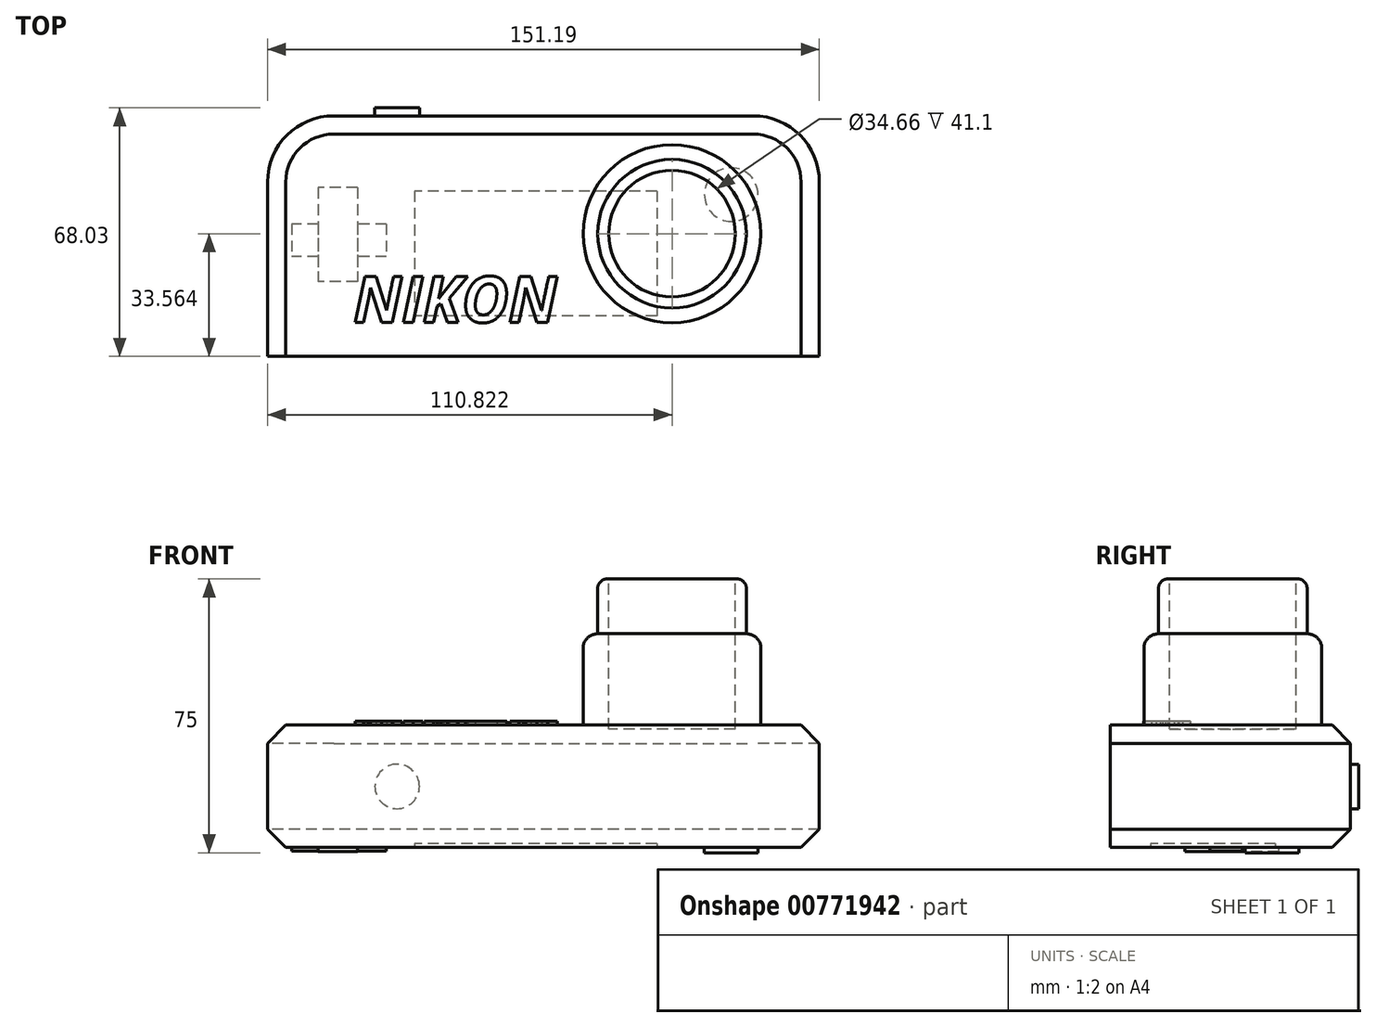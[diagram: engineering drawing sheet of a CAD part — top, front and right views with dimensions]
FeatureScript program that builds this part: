
annotation { "Feature Type Name" : "Feature", "Feature Type Description" : "" }
export const myFeature = defineFeature(function(context is Context, id is Id, definition is map)
    precondition{}
    {
        {
            var Q0;
            Q0=qCreatedBy(makeId("Top.planeOp"),FACE);
            var sketch = newSketch(context, id + "F0", { "sketchPlane" : qUnion([Q0])});
            skLineSegment(sketch, "E0.bottom", {"start": v(0, 0) * mm, "end": v(151.2, 0) * mm});
            skLineSegment(sketch, "E0.top", {"start": v(0, 65.83) * mm, "end": v(151.2, 65.83) * mm});
            skLineSegment(sketch, "E0.left", {"start": v(0, 0) * mm, "end": v(0, 65.83) * mm});
            skLineSegment(sketch, "E0.right", {"start": v(151.2, 0) * mm, "end": v(151.2, 65.83) * mm});
            skSolve(sketch);
        }
        {
            var Q0;
            Q0=makeQuery(id+"F0.imprint","IMPRINT",FACE,{"disambiguationData":[TD([[makeQuery(id+"F0.imprint","IMPRINT",EDGE,{"derivedFrom":sQuery(id+"F0.wireOp",EDGE,"E0.bottom")}),1.0]])]});
            extrude(context, id + "F1", {"entities" : qUnion([Q0]), "depth" : 33.5 * mm, "offsetDistance" : 25 * mm});
        }
        {
            var Q0;
            Q0=makeQuery(id+"F1.opExtrude","CAP_FACE",FACE,{"disambiguationData":[OSD([sQuery(id+"F0.wireOp",EDGE,"E0.bottom"),sQuery(id+"F0.wireOp",EDGE,"E0.top"),sQuery(id+"F0.wireOp",EDGE,"E0.left"),sQuery(id+"F0.wireOp",EDGE,"E0.right")])],"isStart":false});
            var sketch = newSketch(context, id + "F2", { "sketchPlane" : qUnion([Q0])});
            skCircle(sketch, "E1", {"center": v(110.82, 33.56) * mm, "radius": 24.37 * mm});
            skSolve(sketch);
        }
        {
            var Q0;
            Q0 = qSketchRegion(id + "F2", true);
            extrude(context, id + "F3", {"entities" : qUnion([Q0]), "operationType" : NewBodyOperationType.ADD, "depth" : 25 * mm, "offsetDistance" : 25 * mm});
        }
        {
            var Q0;
            Q0=makeQuery(id+"F1.opExtrude","SWEPT_EDGE",EDGE,{"disambiguationData":[OSD([sQuery(id+"F0.wireOp",EDGE,"E0.top"),sQuery(id+"F0.wireOp",EDGE,"E0.right")])]});
            fillet(context, id + "F4", {"entities" : qUnion([Q0]), "radius" : 18.1 * mm, "tangentPropagation" : true, "allowEdgeOverflow" : false});
        }
        {
            var Q0;
            Q0=makeQuery(id+"F1.opExtrude","SWEPT_EDGE",EDGE,{"disambiguationData":[OSD([sQuery(id+"F0.wireOp",EDGE,"E0.top"),sQuery(id+"F0.wireOp",EDGE,"E0.left")])]});
            fillet(context, id + "F5", {"entities" : qUnion([Q0]), "radius" : 18.1 * mm, "tangentPropagation" : true, "allowEdgeOverflow" : false});
        }
        {
            var Q0;
            Q0=makeQuery(id+"F1.opExtrude","CAP_EDGE",EDGE,{"disambiguationData":[OSD([sQuery(id+"F0.wireOp",EDGE,"E0.right")])],"isStart":false});
            var Q1;
            {var subQ0=sQuery(id+"F0.wireOp",EDGE,"E0.right");var subQ1=sQuery(id+"F0.wireOp",EDGE,"E0.top");Q1=makeQuery(id+"F4.opFillet","BLEND_EDGE",EDGE,{"blendedFrom":[makeQuery(id+"F1.opExtrude","SWEPT_EDGE",EDGE,{"disambiguationData":[OSD([subQ1,subQ0])]}),makeQuery(id+"F1.opExtrude","CAP_FACE",FACE,{"disambiguationData":[OSD([sQuery(id+"F0.wireOp",EDGE,"E0.bottom"),subQ1,sQuery(id+"F0.wireOp",EDGE,"E0.left"),subQ0])],"isStart":false})],"blendedInto":[makeQuery(id+"F1.opExtrude","CAP_FACE",FACE,{"disambiguationData":[OSD([sQuery(id+"F0.wireOp",EDGE,"E0.bottom"),subQ1,sQuery(id+"F0.wireOp",EDGE,"E0.left"),subQ0])],"isStart":false})]});}
            var Q2;
            Q2=makeQuery(id+"F1.opExtrude","CAP_EDGE",EDGE,{"disambiguationData":[OSD([sQuery(id+"F0.wireOp",EDGE,"E0.top")])],"isStart":false});
            var Q3;
            {var subQ0=sQuery(id+"F0.wireOp",EDGE,"E0.left");var subQ1=sQuery(id+"F0.wireOp",EDGE,"E0.top");Q3=makeQuery(id+"F5.opFillet","BLEND_EDGE",EDGE,{"blendedFrom":[makeQuery(id+"F1.opExtrude","SWEPT_EDGE",EDGE,{"disambiguationData":[OSD([subQ1,subQ0])]}),makeQuery(id+"F1.opExtrude","CAP_FACE",FACE,{"disambiguationData":[OSD([sQuery(id+"F0.wireOp",EDGE,"E0.bottom"),subQ1,subQ0,sQuery(id+"F0.wireOp",EDGE,"E0.right")])],"isStart":false})],"blendedInto":[makeQuery(id+"F1.opExtrude","CAP_FACE",FACE,{"disambiguationData":[OSD([sQuery(id+"F0.wireOp",EDGE,"E0.bottom"),subQ1,subQ0,sQuery(id+"F0.wireOp",EDGE,"E0.right")])],"isStart":false})]});}
            var Q4;
            Q4=makeQuery(id+"F1.opExtrude","CAP_EDGE",EDGE,{"disambiguationData":[OSD([sQuery(id+"F0.wireOp",EDGE,"E0.left")])],"isStart":false});
            var Q5;
            Q5=makeQuery(id+"F1.opExtrude","CAP_EDGE",EDGE,{"disambiguationData":[OSD([sQuery(id+"F0.wireOp",EDGE,"E0.right")])],"isStart":true});
            var Q6;
            {var subQ0=sQuery(id+"F0.wireOp",EDGE,"E0.right");var subQ1=sQuery(id+"F0.wireOp",EDGE,"E0.top");Q6=makeQuery(id+"F4.opFillet","BLEND_EDGE",EDGE,{"blendedFrom":[makeQuery(id+"F1.opExtrude","SWEPT_EDGE",EDGE,{"disambiguationData":[OSD([subQ1,subQ0])]}),makeQuery(id+"F1.opExtrude","CAP_FACE",FACE,{"disambiguationData":[OSD([sQuery(id+"F0.wireOp",EDGE,"E0.bottom"),subQ1,sQuery(id+"F0.wireOp",EDGE,"E0.left"),subQ0])],"isStart":true})],"blendedInto":[makeQuery(id+"F1.opExtrude","CAP_FACE",FACE,{"disambiguationData":[OSD([sQuery(id+"F0.wireOp",EDGE,"E0.bottom"),subQ1,sQuery(id+"F0.wireOp",EDGE,"E0.left"),subQ0])],"isStart":true})]});}
            var Q7;
            Q7=makeQuery(id+"F1.opExtrude","CAP_EDGE",EDGE,{"disambiguationData":[OSD([sQuery(id+"F0.wireOp",EDGE,"E0.top")])],"isStart":true});
            var Q8;
            Q8=makeQuery(id+"F1.opExtrude","CAP_EDGE",EDGE,{"disambiguationData":[OSD([sQuery(id+"F0.wireOp",EDGE,"E0.left")])],"isStart":true});
            var Q9;
            {var subQ0=sQuery(id+"F0.wireOp",EDGE,"E0.left");var subQ1=sQuery(id+"F0.wireOp",EDGE,"E0.top");Q9=makeQuery(id+"F5.opFillet","BLEND_EDGE",EDGE,{"blendedFrom":[makeQuery(id+"F1.opExtrude","SWEPT_EDGE",EDGE,{"disambiguationData":[OSD([subQ1,subQ0])]}),makeQuery(id+"F1.opExtrude","CAP_FACE",FACE,{"disambiguationData":[OSD([sQuery(id+"F0.wireOp",EDGE,"E0.bottom"),subQ1,subQ0,sQuery(id+"F0.wireOp",EDGE,"E0.right")])],"isStart":true})],"blendedInto":[makeQuery(id+"F1.opExtrude","CAP_FACE",FACE,{"disambiguationData":[OSD([sQuery(id+"F0.wireOp",EDGE,"E0.bottom"),subQ1,subQ0,sQuery(id+"F0.wireOp",EDGE,"E0.right")])],"isStart":true})]});}
            chamfer(context, id + "F6", {"entities" : qUnion([Q0, Q1, Q2, Q3, Q4, Q5, Q6, Q7, Q8, Q9]), "width" : 5 * mm, "tangentPropagation" : true});
        }
        {
            var Q0;
            Q0=makeQuery(id+"F1.opExtrude","CAP_FACE",FACE,{"disambiguationData":[OSD([sQuery(id+"F0.wireOp",EDGE,"E0.bottom"),sQuery(id+"F0.wireOp",EDGE,"E0.top"),sQuery(id+"F0.wireOp",EDGE,"E0.left"),sQuery(id+"F0.wireOp",EDGE,"E0.right")])],"isStart":false});
            var sketch = newSketch(context, id + "F7", { "sketchPlane" : qUnion([Q0])});
            skLineSegment(sketch, "E2.bottom", {"start": v(72.5, 57.52) * mm, "end": v(91.4, 57.52) * mm});
            skLineSegment(sketch, "E2.top", {"start": v(72.5, 48.28) * mm, "end": v(91.4, 48.28) * mm});
            skLineSegment(sketch, "E2.left", {"start": v(72.5, 57.52) * mm, "end": v(72.5, 48.28) * mm});
            skLineSegment(sketch, "E2.right", {"start": v(91.4, 57.52) * mm, "end": v(91.4, 48.28) * mm});
            skSolve(sketch);
        }
        {
            var Q0;
            Q0=makeQuery(id+"F1.opExtrude","CAP_FACE",FACE,{"disambiguationData":[OSD([sQuery(id+"F0.wireOp",EDGE,"E0.bottom"),sQuery(id+"F0.wireOp",EDGE,"E0.top"),sQuery(id+"F0.wireOp",EDGE,"E0.left"),sQuery(id+"F0.wireOp",EDGE,"E0.right")])],"isStart":true});
            var sketch = newSketch(context, id + "F8", { "sketchPlane" : qUnion([Q0])});
            skLineSegment(sketch, "E3.bottom", {"start": v(106.7, -45.26) * mm, "end": v(40.25, -45.26) * mm});
            skLineSegment(sketch, "E3.top", {"start": v(106.7, -11) * mm, "end": v(40.25, -11) * mm});
            skLineSegment(sketch, "E3.left", {"start": v(106.7, -45.26) * mm, "end": v(106.7, -11) * mm});
            skLineSegment(sketch, "E3.right", {"start": v(40.25, -45.26) * mm, "end": v(40.25, -11) * mm});
            skSolve(sketch);
        }
        {
            var Q0;
            Q0=makeQuery(id+"F8.imprint","IMPRINT",FACE,{"disambiguationData":[TD([[makeQuery(id+"F8.imprint","IMPRINT",EDGE,{"derivedFrom":sQuery(id+"F8.wireOp",EDGE,"E3.bottom")}),-1.0]])]});
            extrude(context, id + "F9", {"entities" : qUnion([Q0]), "operationType" : NewBodyOperationType.REMOVE, "oppositeDirection" : true, "depth" : 1 * mm, "offsetDistance" : 25 * mm});
        }
        {
            var Q0;
            Q0=makeQuery(id+"F3.opExtrude","CAP_EDGE",EDGE,{"disambiguationData":[OSD([sQuery(id+"F2.wireOp",EDGE,"E1")])],"isStart":false});
            fillet(context, id + "F10", {"entities" : qUnion([Q0]), "radius" : 4 * mm, "tangentPropagation" : true, "allowEdgeOverflow" : false});
        }
        {
            var Q0;
            Q0=makeQuery(id+"F3.opExtrude","CAP_FACE",FACE,{"disambiguationData":[OSD([sQuery(id+"F2.wireOp",EDGE,"E1")])],"isStart":false});
            var sketch = newSketch(context, id + "F11", { "sketchPlane" : qUnion([Q0])});
            skCircle(sketch, "E4", {"center": v(110.82, 33.56) * mm, "radius": 20.35 * mm});
            skSolve(sketch);
        }
        {
            var Q0;
            Q0 = qSketchRegion(id + "F11", true);
            extrude(context, id + "F12", {"entities" : qUnion([Q0]), "operationType" : NewBodyOperationType.ADD, "depth" : 15 * mm, "offsetDistance" : 25 * mm});
        }
        {
            var Q0;
            Q0=makeQuery(id+"F12.opExtrude","CAP_EDGE",EDGE,{"disambiguationData":[OSD([sQuery(id+"F11.wireOp",EDGE,"E4")])],"isStart":false});
            fillet(context, id + "F13", {"entities" : qUnion([Q0]), "radius" : 2.5 * mm, "tangentPropagation" : true, "allowEdgeOverflow" : false});
        }
        {
            var Q0;
            Q0=makeQuery(id+"F12.opExtrude","CAP_FACE",FACE,{"disambiguationData":[OSD([sQuery(id+"F11.wireOp",EDGE,"E4")])],"isStart":false});
            var sketch = newSketch(context, id + "F14", { "sketchPlane" : qUnion([Q0])});
            skCircle(sketch, "E5", {"center": v(110.82, 33.56) * mm, "radius": 17.33 * mm});
            skSolve(sketch);
        }
        {
            var Q0;
            Q0 = qSketchRegion(id + "F14", true);
            extrude(context, id + "F15", {"entities" : qUnion([Q0]), "operationType" : NewBodyOperationType.REMOVE, "oppositeDirection" : true, "depth" : 41.1 * mm, "offsetDistance" : 25 * mm});
        }
        {
            var Q0;
            Q0=makeQuery(id+"F1.opExtrude","CAP_FACE",FACE,{"disambiguationData":[OSD([sQuery(id+"F0.wireOp",EDGE,"E0.bottom"),sQuery(id+"F0.wireOp",EDGE,"E0.top"),sQuery(id+"F0.wireOp",EDGE,"E0.left"),sQuery(id+"F0.wireOp",EDGE,"E0.right")])],"isStart":true});
            var sketch = newSketch(context, id + "F16", { "sketchPlane" : qUnion([Q0])});
            skSolve(sketch);
        }
        {
            var Q0;
            {var subQ3=sQuery(id+"F0.wireOp",EDGE,"E0.bottom");Q0=makeQuery(id+"F16.imprint","IMPRINT",FACE,{"disambiguationData":[TD([[makeQuery(id+"F16.imprint","IMPRINT",EDGE,{"derivedFrom":makeQuery(id+"F1.opExtrude","CAP_EDGE",EDGE,{"disambiguationData":[OSD([subQ3])],"isStart":true})}),-1.0]])]});}
            var sketch = newSketch(context, id + "F17", { "sketchPlane" : qUnion([Q0])});
            skCircle(sketch, "E6", {"center": v(127.03, -44.28) * mm, "radius": 7.34 * mm});
            skSolve(sketch);
        }
        {
            var Q0;
            Q0 = qSketchRegion(id + "F17", true);
            extrude(context, id + "F18", {"entities" : qUnion([Q0]), "operationType" : NewBodyOperationType.ADD, "depth" : 1.5 * mm, "offsetDistance" : 25 * mm});
        }
        {
            var Q0;
            {var subQ3=sQuery(id+"F0.wireOp",EDGE,"E0.bottom");Q0=makeQuery(id+"F16.imprint","IMPRINT",FACE,{"disambiguationData":[TD([[makeQuery(id+"F16.imprint","IMPRINT",EDGE,{"derivedFrom":makeQuery(id+"F1.opExtrude","CAP_EDGE",EDGE,{"disambiguationData":[OSD([subQ3])],"isStart":true})}),-1.0]])]});}
            var sketch = newSketch(context, id + "F19", { "sketchPlane" : qUnion([Q0])});
            skLineSegment(sketch, "E7.bottom", {"start": v(24.65, -46.19) * mm, "end": v(13.89, -46.19) * mm});
            skLineSegment(sketch, "E7.top", {"start": v(24.65, -20.42) * mm, "end": v(13.89, -20.42) * mm});
            skLineSegment(sketch, "E7.left", {"start": v(24.65, -46.19) * mm, "end": v(24.65, -20.42) * mm});
            skLineSegment(sketch, "E7.right", {"start": v(13.89, -46.19) * mm, "end": v(13.89, -20.42) * mm});
            skSolve(sketch);
        }
        {
            var Q0;
            Q0 = qSketchRegion(id + "F19", true);
            extrude(context, id + "F20", {"entities" : qUnion([Q0]), "operationType" : NewBodyOperationType.ADD, "depth" : 1.1 * mm, "offsetDistance" : 25 * mm});
        }
        {
            var Q0;
            {var subQ3=sQuery(id+"F0.wireOp",EDGE,"E0.bottom");Q0=makeQuery(id+"F16.imprint","IMPRINT",FACE,{"disambiguationData":[TD([[makeQuery(id+"F16.imprint","IMPRINT",EDGE,{"derivedFrom":makeQuery(id+"F1.opExtrude","CAP_EDGE",EDGE,{"disambiguationData":[OSD([subQ3])],"isStart":true})}),-1.0]])]});}
            var sketch = newSketch(context, id + "F21", { "sketchPlane" : qUnion([Q0])});
            skLineSegment(sketch, "E8.bottom", {"start": v(32.54, -36.24) * mm, "end": v(6.6, -36.24) * mm});
            skLineSegment(sketch, "E8.top", {"start": v(32.54, -27.32) * mm, "end": v(6.6, -27.32) * mm});
            skLineSegment(sketch, "E8.left", {"start": v(32.54, -36.24) * mm, "end": v(32.54, -27.32) * mm});
            skLineSegment(sketch, "E8.right", {"start": v(6.6, -36.24) * mm, "end": v(6.6, -27.32) * mm});
            skSolve(sketch);
        }
        {
            var Q0;
            Q0 = qSketchRegion(id + "F21", true);
            extrude(context, id + "F22", {"entities" : qUnion([Q0]), "operationType" : NewBodyOperationType.ADD, "depth" : 1 * mm, "offsetDistance" : 25 * mm});
        }
        {
            var Q0;
            Q0=makeQuery(id+"F1.opExtrude","SWEPT_FACE",FACE,{"disambiguationData":[OSD([sQuery(id+"F0.wireOp",EDGE,"E0.top")])]});
            var sketch = newSketch(context, id + "F23", { "sketchPlane" : qUnion([Q0])});
            skCircle(sketch, "E9", {"center": v(-35.51, 16.69) * mm, "radius": 6.1 * mm});
            skSolve(sketch);
        }
        {
            var Q0;
            Q0 = qSketchRegion(id + "F23", true);
            extrude(context, id + "F24", {"entities" : qUnion([Q0]), "operationType" : NewBodyOperationType.ADD, "depth" : 2.2 * mm, "offsetDistance" : 25 * mm});
        }
        {
            var Q0;
            Q0=makeQuery(id+"F7.imprint","IMPRINT",FACE,{"disambiguationData":[TD([[makeQuery(id+"F7.imprint","IMPRINT",EDGE,{"derivedFrom":sQuery(id+"F7.wireOp",EDGE,"E2.bottom")}),1.0]])]});
            var sketch = newSketch(context, id + "F25", { "sketchPlane" : qUnion([Q0])});
            skText(sketch, "E10", { "text": "NIKON", "fontName": "OpenSans-BoldItalic.ttf"});
            const initialGuessF25  = {"E10": [0.02353, 0.00927, 1, 0, 0.01265]};
            skSetInitialGuess(sketch, initialGuessF25);
            skSolve(sketch);
        }
        {
            var Q0;
            Q0 = qSketchRegion(id + "F25", true);
            extrude(context, id + "F26", {"entities" : qUnion([Q0]), "operationType" : NewBodyOperationType.ADD, "depth" : 1 * mm, "offsetDistance" : 25 * mm});
        }
    });
